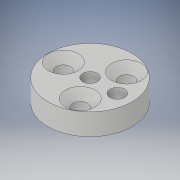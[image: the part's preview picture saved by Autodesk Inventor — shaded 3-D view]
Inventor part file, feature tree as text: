
AUTODESK INVENTOR PART (.ipt)
format: ipt  version: 2019 (Build 230136000, 136)  size: 126,976 bytes
history: native  units: mm
features: sketch x3, hole x2, other x1, extrude x1
ambient origin geometry x8: Origin, YZ Plane, XZ Plane, XY Plane, X Axis, Y Axis, Z Axis, Center Point
bodies: Body1 (feature_tree)
feature tree (7):
  other  "Bryła1"
  extrude  "Wyciągnięcie proste1"  Depth=19.5mm
  hole  "Otwór1"  [1 undecoded]
  hole  "Otwór2"  [1 undecoded]
  sketch  "Szkic1"
  sketch  "Szkic2"
  sketch  "Szkic3"
note: 2 required parameter values undecoded (feature->parameter linkage not recoverable at this tier; creation-order binding heuristic only, values carry confidence <= 0.55)
